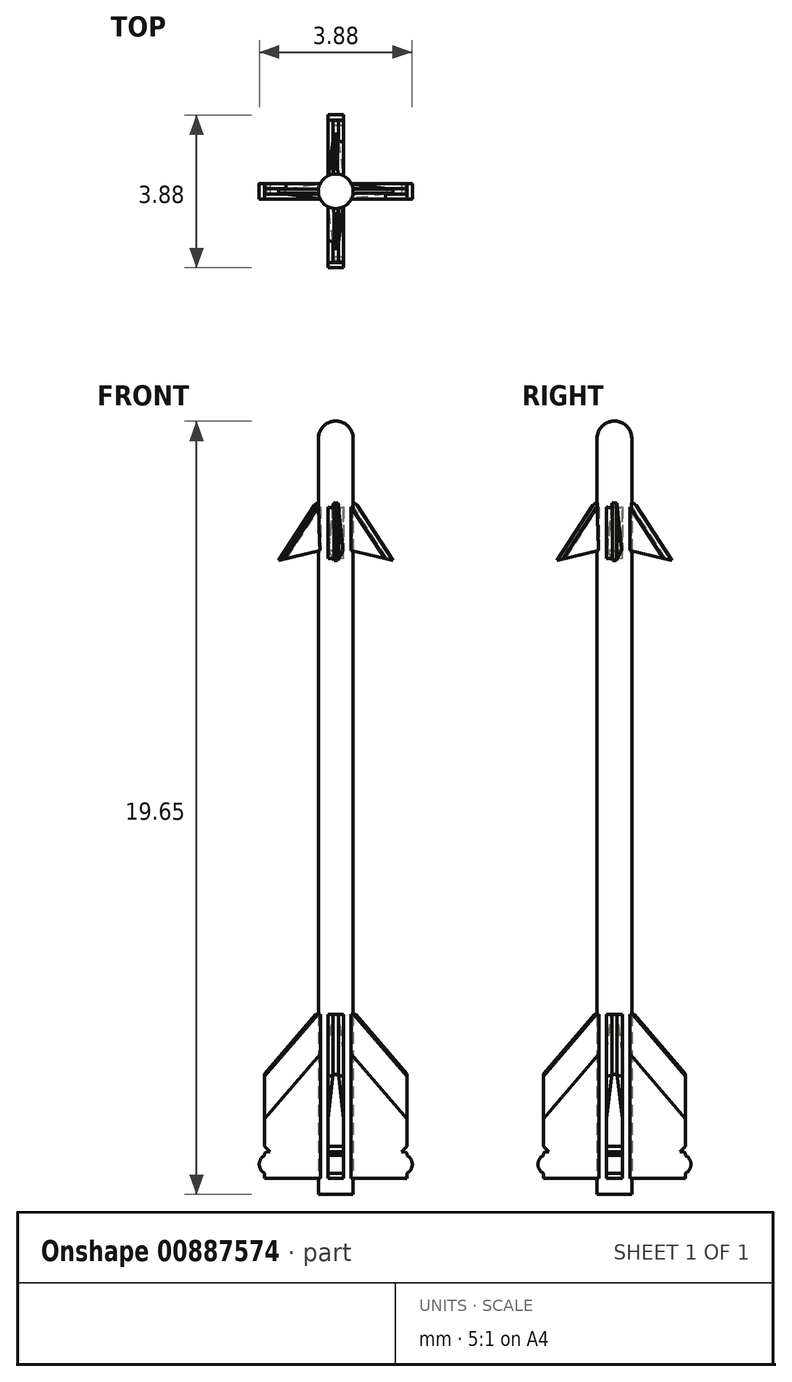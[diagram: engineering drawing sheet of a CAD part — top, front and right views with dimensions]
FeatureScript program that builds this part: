
annotation { "Feature Type Name" : "Feature", "Feature Type Description" : "" }
export const myFeature = defineFeature(function(context is Context, id is Id, definition is map)
    precondition{}
    {
        {
            var Q0;
            Q0=qCreatedBy(makeId("Front.planeOp"),FACE);
            var sketch = newSketch(context, id + "F0", { "sketchPlane" : qUnion([Q0])});
            skLineSegment(sketch, "E0", {"start": v(0, 0) * mm, "end": v(0, 19.65) * mm});
            skLineSegment(sketch, "E1", {"start": v(0.44, 19.21) * mm, "end": v(0.44, 0) * mm});
            skLineSegment(sketch, "E2", {"start": v(0.44, 0) * mm, "end": v(0, 0) * mm});
            skArc(sketch, "E3", {"start": v(0.44, 19.21) * mm, "mid": v(0.31, 19.52) * mm, "end": v(0, 19.65) * mm});
            skLineSegment(sketch, "E4", {"start": v(0, 19.65) * mm, "end": v(1.85, 19.65) * mm, "construction": true});
            skSolve(sketch);
        }
        {
            var Q0;
            Q0=qSketchRegion(id+"F0",true);
            var Q1;
            Q1=sQuery(id+"F0.wireOp",EDGE,"E0");
            revolve(context, id + "F1", {"surfaceOperationType" : NewSurfaceOperationType.NEW, "entities" : qUnion([Q0]), "axis" : qUnion([Q1]), "revolveType" : RevolveType.FULL});
        }
        {
            var Q0;
            Q0=qCreatedBy(makeId("Front.planeOp"),FACE);
            var sketch = newSketch(context, id + "F2", { "sketchPlane" : qUnion([Q0])});
            skLineSegment(sketch, "E5", {"start": v(0.65, 4.58) * mm, "end": v(-0.65, 4.58) * mm});
            skLineSegment(sketch, "E6", {"start": v(-1.8, 3.23) * mm, "end": v(-0.65, 4.58) * mm});
            skLineSegment(sketch, "E7", {"start": v(-1.8, 3.23) * mm, "end": v(-1.8, 1.23) * mm});
            skLineSegment(sketch, "E8", {"start": v(1.8, 1.23) * mm, "end": v(1.8, 3.23) * mm});
            skLineSegment(sketch, "E9", {"start": v(0.65, 4.58) * mm, "end": v(1.8, 3.23) * mm});
            skLineSegment(sketch, "E10", {"start": v(0, 0) * mm, "end": v(0, 4.58) * mm, "construction": true});
            skLineSegment(sketch, "E11", {"start": v(-0.44, 0.8) * mm, "end": v(-0.44, 4.16) * mm, "construction": true});
            skLineSegment(sketch, "E12.0", {"start": v(0.44, 19.21) * mm, "end": v(-0.44, 19.21) * mm});
            skLineSegment(sketch, "E13", {"start": v(-1.8, 0.42) * mm, "end": v(-1.8, 0.54) * mm});
            skLineSegment(sketch, "E14", {"start": v(1.8, 0.42) * mm, "end": v(1.8, 0.54) * mm});
            skLineSegment(sketch, "E15", {"start": v(1.8, 1.23) * mm, "end": v(1.67, 1.1) * mm});
            skLineSegment(sketch, "E16", {"start": v(1.8, 1.05) * mm, "end": v(1.8, 1) * mm});
            skLineSegment(sketch, "E17", {"start": v(-1.8, 1.23) * mm, "end": v(-1.67, 1.1) * mm});
            skLineSegment(sketch, "E18", {"start": v(-1.8, 1.05) * mm, "end": v(-1.8, 1) * mm});
            skArc(sketch, "E19", {"start": v(-1.8, 1) * mm, "mid": v(-1.94, 0.77) * mm, "end": v(-1.8, 0.54) * mm});
            skArc(sketch, "E20", {"start": v(1.8, 0.54) * mm, "mid": v(1.94, 0.77) * mm, "end": v(1.8, 1) * mm});
            skLineSegment(sketch, "E21", {"start": v(-1.8, 1.05) * mm, "end": v(-1.76, 1.1) * mm});
            skLineSegment(sketch, "E22", {"start": v(-1.76, 1.1) * mm, "end": v(-1.67, 1.1) * mm});
            skLineSegment(sketch, "E23", {"start": v(1.8, 1.05) * mm, "end": v(1.76, 1.1) * mm});
            skLineSegment(sketch, "E24", {"start": v(1.76, 1.1) * mm, "end": v(1.67, 1.1) * mm});
            skLineSegment(sketch, "E25", {"start": v(-1.8, 0.42) * mm, "end": v(1.8, 0.42) * mm});
            skLineSegment(sketch, "E26", {"start": v(0, 0) * mm, "end": v(0, 0.42) * mm, "construction": true});
            skLineSegment(sketch, "E27.0", {"start": v(0.44, 0) * mm, "end": v(-0.44, 0) * mm});
            skLineSegment(sketch, "E28", {"start": v(-1.46, 16.11) * mm, "end": v(0, 16.46) * mm});
            skLineSegment(sketch, "E29", {"start": v(0, 16.46) * mm, "end": v(1.46, 16.11) * mm});
            skLineSegment(sketch, "E30", {"start": v(1.46, 16.11) * mm, "end": v(0.55, 17.51) * mm});
            skLineSegment(sketch, "E31", {"start": v(-0.55, 17.51) * mm, "end": v(-1.46, 16.11) * mm});
            skLineSegment(sketch, "E32", {"start": v(-0.44, 17.57) * mm, "end": v(0.44, 17.57) * mm});
            skArc(sketch, "E33", {"start": v(-0.44, 17.57) * mm, "mid": v(-0.5, 17.55) * mm, "end": v(-0.55, 17.51) * mm});
            skArc(sketch, "E34", {"start": v(0.55, 17.51) * mm, "mid": v(0.5, 17.55) * mm, "end": v(0.44, 17.57) * mm});
            skPoint(sketch, "E35", {"position": v(-0.44, 16.35) * mm});
            skSolve(sketch);
        }
        {
            var Q0;
            Q0=qSketchRegion(id+"F2",true);
            extrude(context, id + "F3", {"entities" : qUnion([Q0]), "operationType" : NewBodyOperationType.ADD, "depth" : .4 * mm, "offsetDistance" : 25 * mm, "symmetric" : true});
        }
        {
            var Q0;
            Q0=makeQuery(id+"F3.opExtrude","CAP_EDGE",EDGE,{"disambiguationData":[OSD([sQuery(id+"F2.wireOp",EDGE,"E30")])],"isStart":false});
            var Q1;
            Q1=makeQuery(id+"F3.opExtrude","CAP_EDGE",EDGE,{"disambiguationData":[OSD([sQuery(id+"F2.wireOp",EDGE,"E30")])],"isStart":true});
            var Q2;
            Q2=makeQuery(id+"F3.opExtrude","CAP_EDGE",EDGE,{"disambiguationData":[OSD([sQuery(id+"F2.wireOp",EDGE,"E31")])],"isStart":false});
            var Q3;
            Q3=makeQuery(id+"F3.opExtrude","CAP_EDGE",EDGE,{"disambiguationData":[OSD([sQuery(id+"F2.wireOp",EDGE,"E6")])],"isStart":true});
            var Q4;
            Q4=makeQuery(id+"F3.opExtrude","CAP_EDGE",EDGE,{"disambiguationData":[OSD([sQuery(id+"F2.wireOp",EDGE,"E9")])],"isStart":true});
            chamfer(context, id + "F4", {"entities" : qUnion([Q0, Q1, Q2, Q3, Q4]), "chamferType" : ChamferType.OFFSET_ANGLE, "width" : .15 * mm, "oppositeDirection" : true, "angle" : 80 * degree});
        }
        {
            var Q0;
            Q0=makeQuery(id+"F3.opExtrude","CAP_EDGE",EDGE,{"disambiguationData":[OSD([sQuery(id+"F2.wireOp",EDGE,"E9")])],"isStart":false});
            var Q1;
            Q1=makeQuery(id+"F3.opExtrude","CAP_EDGE",EDGE,{"disambiguationData":[OSD([sQuery(id+"F2.wireOp",EDGE,"E31")])],"isStart":true});
            var Q2;
            Q2=makeQuery(id+"F3.opExtrude","CAP_EDGE",EDGE,{"disambiguationData":[OSD([sQuery(id+"F2.wireOp",EDGE,"E6")])],"isStart":false});
            chamfer(context, id + "F5", {"entities" : qUnion([Q0, Q1, Q2]), "chamferType" : ChamferType.OFFSET_ANGLE, "width" : .15 * mm, "oppositeDirection" : false, "angle" : 80 * degree});
        }
        {
            var Q0;
            Q0=makeQuery(id+"F1.opRevolve","SWEPT_BODY",BODY,{"disambiguationData":[OSD([sQuery(id+"F0.wireOp",EDGE,"E0"),sQuery(id+"F0.wireOp",EDGE,"E1"),sQuery(id+"F0.wireOp",EDGE,"E2"),sQuery(id+"F0.wireOp",EDGE,"E3")])]});
            var Q1;
            Q1=makeQuery(id+"F1.opRevolve","SWEPT_FACE",FACE,{"disambiguationData":[OSD([sQuery(id+"F0.wireOp",EDGE,"E1")])]});
            circularPattern(context, id + "F6", {"entities" : qUnion([Q0]), "axis" : qUnion([Q1]), "angle" : 360 * degree, "instanceCount" : 4, "equalSpace" : true, "computeTransformsWithoutBuiltin" : true});
        }
    });
